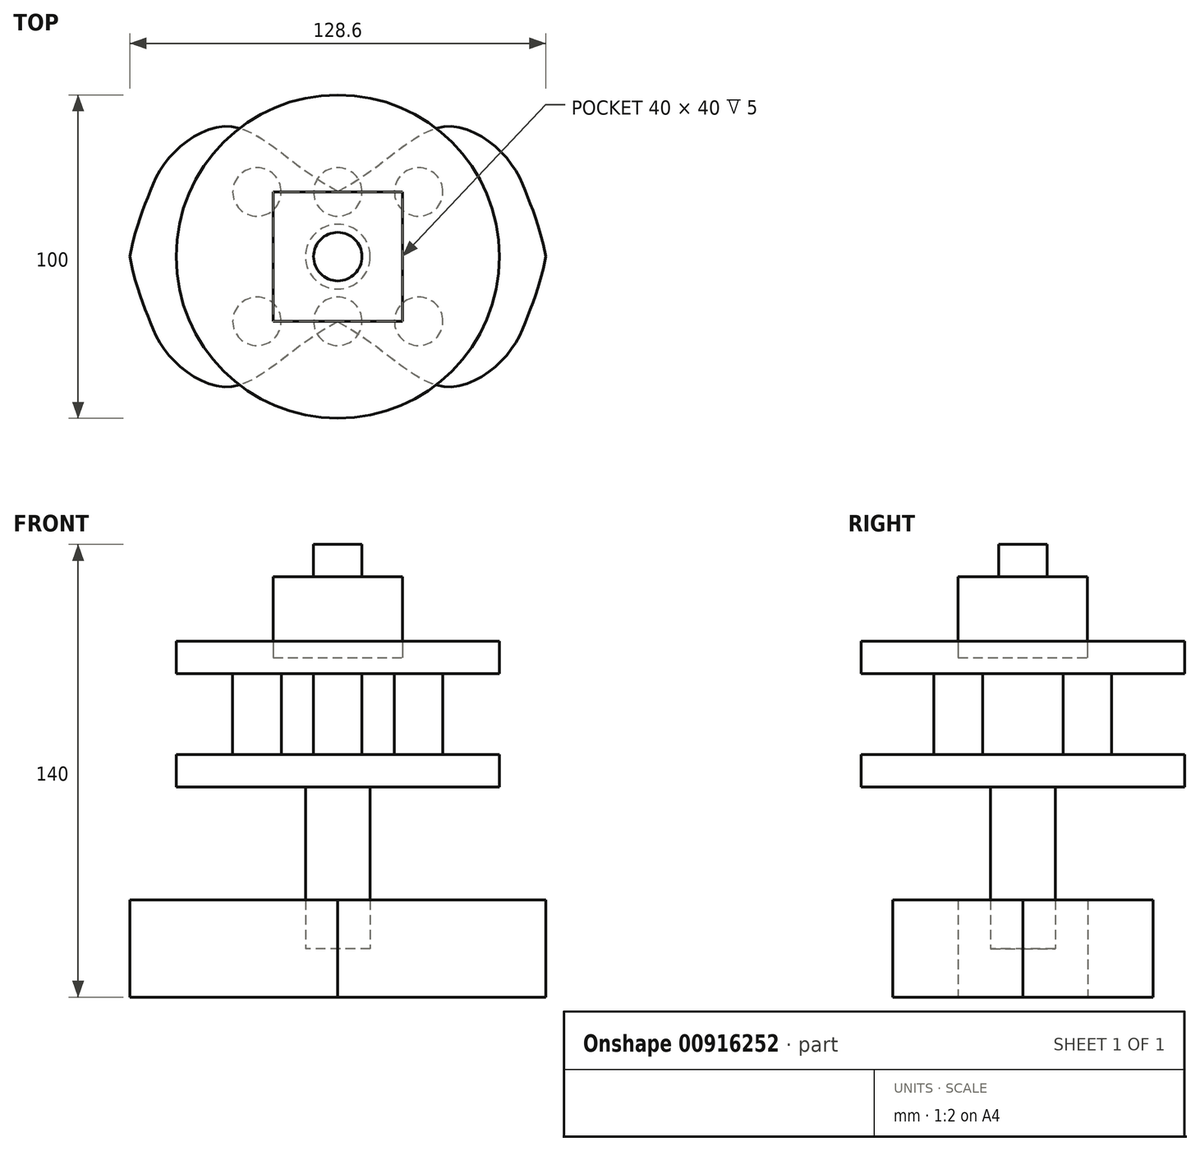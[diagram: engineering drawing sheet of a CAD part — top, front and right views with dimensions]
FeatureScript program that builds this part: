
annotation { "Feature Type Name" : "Feature", "Feature Type Description" : "" }
export const myFeature = defineFeature(function(context is Context, id is Id, definition is map)
    precondition{}
    {
        {
            var Q0;
            Q0=qCreatedBy(makeId("Top.planeOp"),FACE);
            var sketch = newSketch(context, id + "F0", { "sketchPlane" : qUnion([Q0])});
            skFitSpline(sketch, "E0", {"points": [v(0, 20.08) * mm, v(-14.26, 29.58) * mm, v(-21.82, 35.2) * mm, v(-33.27, 40.25) * mm, v(-45.68, 36.37) * mm, v(-54.99, 26.67) * mm, v(-59.45, 16.58) * mm, v(-64.3, 0) * mm], "startDerivative": vector(-138, 78.85) * mm, "endDerivative": vector(-28.73, -152.63) * mm});
            skFitSpline(sketch, "E1.MirrorCS", {"points": [v(0, 20.08) * mm, v(14.26, 29.58) * mm, v(21.82, 35.2) * mm, v(33.27, 40.25) * mm, v(45.68, 36.37) * mm, v(54.99, 26.67) * mm, v(59.45, 16.58) * mm, v(64.3, 0) * mm], "startDerivative": vector(138, 78.85) * mm, "endDerivative": vector(28.73, -152.63) * mm});
            skFitSpline(sketch, "E2.MirrorCS", {"points": [v(0, -20.08) * mm, v(-14.26, -29.58) * mm, v(-21.82, -35.2) * mm, v(-33.27, -40.25) * mm, v(-45.68, -36.37) * mm, v(-54.99, -26.67) * mm, v(-59.45, -16.58) * mm, v(-64.3, 0) * mm], "startDerivative": vector(-138, -78.85) * mm, "endDerivative": vector(-28.73, 152.63) * mm});
            skFitSpline(sketch, "E3.MirrorCS", {"points": [v(0, -20.08) * mm, v(14.26, -29.58) * mm, v(21.82, -35.2) * mm, v(33.27, -40.25) * mm, v(45.68, -36.37) * mm, v(54.99, -26.67) * mm, v(59.45, -16.58) * mm, v(64.3, 0) * mm], "startDerivative": vector(138, -78.85) * mm, "endDerivative": vector(28.73, 152.63) * mm});
            skSolve(sketch);
        }
        {
            var Q0;
            Q0 = qSketchRegion(id + "F0", true);
            extrude(context, id + "F1", {"entities" : qUnion([Q0]), "endBound" : BoundingType.SYMMETRIC, "depth" : 30 * mm, "offsetDistance" : 25 * mm});
        }
        {
            var Q0;
            Q0=qCreatedBy(makeId("Top.planeOp"),FACE);
            var sketch = newSketch(context, id + "F2", { "sketchPlane" : qUnion([Q0])});
            skCircle(sketch, "E4", {"center": v(0, 0) * mm, "radius": 10 * mm});
            skSolve(sketch);
        }
        {
            var Q0;
            Q0 = qSketchRegion(id + "F2", true);
            extrude(context, id + "F3", {"entities" : qUnion([Q0]), "depth" : 50 * mm, "offsetDistance" : 25 * mm});
        }
        {
            var Q0;
            Q0=makeQuery(id+"F3.opExtrude","SWEPT_BODY",BODY,{"disambiguationData":[OSD([sQuery(id+"F2.wireOp",EDGE,"E4")])]});
            var Q1;
            Q1=makeQuery(id+"F1.opExtrude","SWEPT_BODY",BODY,{"disambiguationData":[OSD([sQuery(id+"F0.wireOp",EDGE,"E0"),sQuery(id+"F0.wireOp",EDGE,"E1.MirrorCS"),sQuery(id+"F0.wireOp",EDGE,"E2.MirrorCS"),sQuery(id+"F0.wireOp",EDGE,"E3.MirrorCS")])]});
            booleanBodies(context, id + "F4", {"operationType" : BooleanOperationType.SUBTRACTION, "tools" : qUnion([Q0]), "targets" : qUnion([Q1]), "keepTools" : true});
        }
        {
            var Q0;
            Q0=makeQuery(id+"F3.opExtrude","CAP_FACE",FACE,{"disambiguationData":[OSD([sQuery(id+"F2.wireOp",EDGE,"E4")])],"isStart":false});
            var sketch = newSketch(context, id + "F5", { "sketchPlane" : qUnion([Q0])});
            skCircle(sketch, "E5", {"center": v(0, 0) * mm, "radius": 50 * mm});
            skSolve(sketch);
        }
        {
            var Q0;
            Q0 = qSketchRegion(id + "F5", true);
            extrude(context, id + "F6", {"entities" : qUnion([Q0]), "operationType" : NewBodyOperationType.ADD, "depth" : 10 * mm, "offsetDistance" : 25 * mm});
        }
        {
            var Q0;
            Q0=makeQuery(id+"F6.opExtrude","CAP_FACE",FACE,{"disambiguationData":[OSD([sQuery(id+"F5.wireOp",EDGE,"E5")])],"isStart":false});
            var sketch = newSketch(context, id + "F7", { "sketchPlane" : qUnion([Q0])});
            skCircle(sketch, "E6", {"center": v(-25, 20) * mm, "radius": 7.5 * mm});
            skCircle(sketch, "E7.1.0.0", {"center": v(0, 20) * mm, "radius": 7.5 * mm});
            skCircle(sketch, "E7.2.0.0", {"center": v(25, 20) * mm, "radius": 7.5 * mm});
            skLineSegment(sketch, "E7.direction1", {"start": v(-25, 20) * mm, "end": v(0, 20) * mm, "construction": true});
            skCircle(sketch, "E8.MirrorC", {"center": v(25, -20) * mm, "radius": 7.5 * mm});
            skCircle(sketch, "E9.MirrorC", {"center": v(0, -20) * mm, "radius": 7.5 * mm});
            skCircle(sketch, "E10.MirrorC", {"center": v(-25, -20) * mm, "radius": 7.5 * mm});
            skSolve(sketch);
        }
        {
            var Q0;
            Q0 = qSketchRegion(id + "F7", true);
            extrude(context, id + "F8", {"entities" : qUnion([Q0]), "operationType" : NewBodyOperationType.ADD, "depth" : 25 * mm, "offsetDistance" : 25 * mm});
        }
        {
            var Q0;
            Q0=makeQuery(id+"F8.opExtrude","CAP_FACE",FACE,{"disambiguationData":[OSD([sQuery(id+"F7.wireOp",EDGE,"E9.MirrorC")])],"isStart":false});
            cPlane(context, id + "F9", {"entities" : qUnion([Q0]), "cplaneType" : CPlaneType.OFFSET, "offset" : 0 * mm, "width" : 150 * mm, "height" : 150 * mm});
        }
        {
            var Q0;
            Q0=qCreatedBy(id+"F9.planeOp",FACE);
            var sketch = newSketch(context, id + "F10", { "sketchPlane" : qUnion([Q0])});
            skCircle(sketch, "E11", {"center": v(0, 0) * mm, "radius": 50 * mm});
            skSolve(sketch);
        }
        {
            var Q0;
            Q0 = qSketchRegion(id + "F10", true);
            extrude(context, id + "F11", {"entities" : qUnion([Q0]), "operationType" : NewBodyOperationType.ADD, "depth" : 10 * mm, "offsetDistance" : 25 * mm});
        }
        {
            var Q0;
            Q0=makeQuery(id+"F11.opExtrude","CAP_FACE",FACE,{"disambiguationData":[OSD([sQuery(id+"F10.wireOp",EDGE,"E11")])],"isStart":false});
            cPlane(context, id + "F12", {"entities" : qUnion([Q0]), "cplaneType" : CPlaneType.OFFSET, "offset" : 5 * mm, "oppositeDirection" : true, "width" : 150 * mm, "height" : 150 * mm});
        }
        {
            var Q0;
            Q0=qCreatedBy(id+"F12.planeOp",FACE);
            var sketch = newSketch(context, id + "F13", { "sketchPlane" : qUnion([Q0])});
            skLineSegment(sketch, "E12.bottom", {"start": v(-20, -20) * mm, "end": v(20, -20) * mm});
            skLineSegment(sketch, "E12.top", {"start": v(-20, 20) * mm, "end": v(20, 20) * mm});
            skLineSegment(sketch, "E12.left", {"start": v(-20, -20) * mm, "end": v(-20, 20) * mm});
            skLineSegment(sketch, "E12.right", {"start": v(20, -20) * mm, "end": v(20, 20) * mm});
            skPoint(sketch, "E12.middle", {"position": v(0, 0) * mm});
            skSolve(sketch);
        }
        {
            var Q0;
            Q0 = qSketchRegion(id + "F13", true);
            extrude(context, id + "F14", {"entities" : qUnion([Q0]), "depth" : 25 * mm, "offsetDistance" : 25 * mm});
        }
        {
            var Q0;
            Q0=makeQuery(id+"F14.opExtrude","SWEPT_BODY",BODY,{"disambiguationData":[OSD([sQuery(id+"F13.wireOp",EDGE,"E12.bottom"),sQuery(id+"F13.wireOp",EDGE,"E12.top"),sQuery(id+"F13.wireOp",EDGE,"E12.left"),sQuery(id+"F13.wireOp",EDGE,"E12.right")])]});
            var Q1;
            Q1=makeQuery(id+"F3.opExtrude","SWEPT_BODY",BODY,{"disambiguationData":[OSD([sQuery(id+"F2.wireOp",EDGE,"E4")])]});
            booleanBodies(context, id + "F15", {"operationType" : BooleanOperationType.SUBTRACTION, "tools" : qUnion([Q0]), "targets" : qUnion([Q1]), "keepTools" : true});
        }
        {
            var Q0;
            Q0=makeQuery(id+"F14.opExtrude","CAP_FACE",FACE,{"disambiguationData":[OSD([sQuery(id+"F13.wireOp",EDGE,"E12.bottom"),sQuery(id+"F13.wireOp",EDGE,"E12.top"),sQuery(id+"F13.wireOp",EDGE,"E12.left"),sQuery(id+"F13.wireOp",EDGE,"E12.right")])],"isStart":false});
            var sketch = newSketch(context, id + "F16", { "sketchPlane" : qUnion([Q0])});
            skCircle(sketch, "E13", {"center": v(0, 0) * mm, "radius": 7.5 * mm});
            skSolve(sketch);
        }
        {
            var Q0;
            Q0 = qSketchRegion(id + "F16", true);
            extrude(context, id + "F17", {"entities" : qUnion([Q0]), "operationType" : NewBodyOperationType.ADD, "depth" : 10 * mm, "offsetDistance" : 25 * mm});
        }
    });
